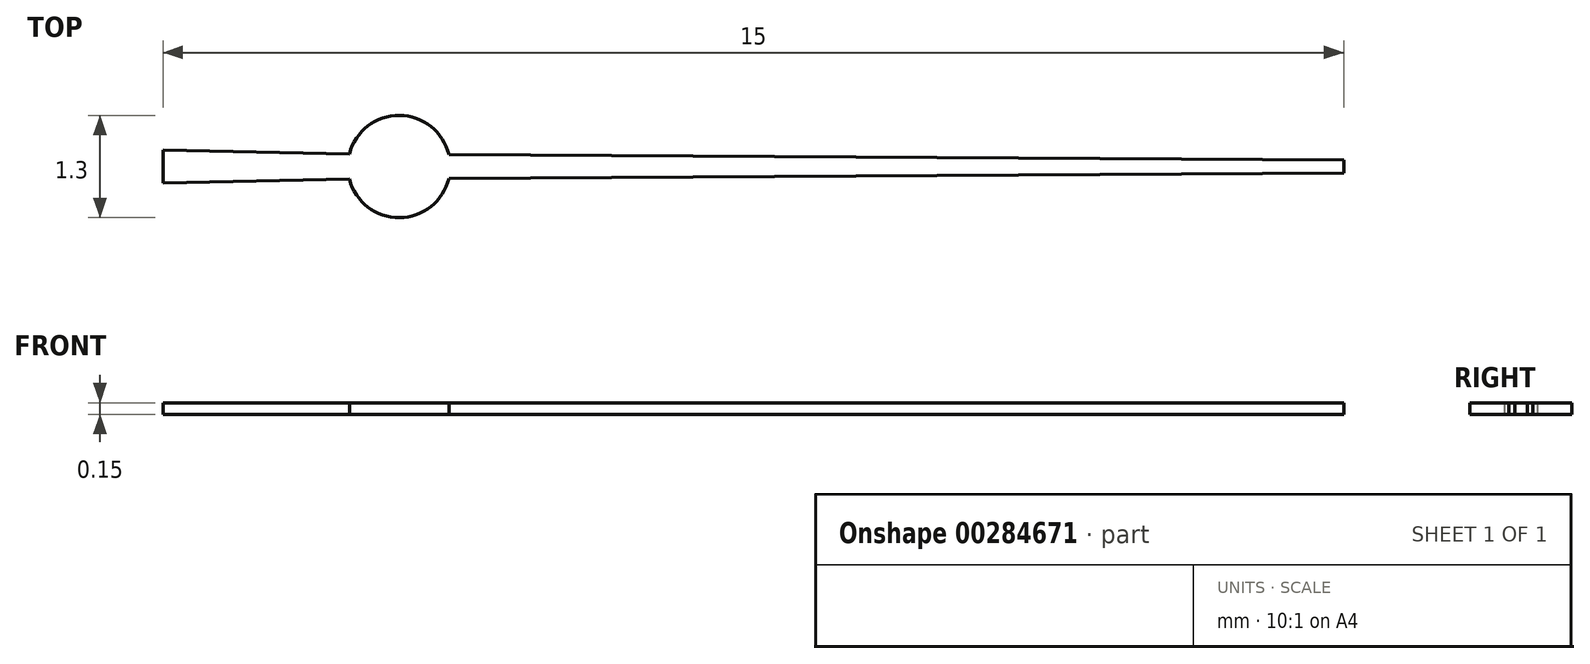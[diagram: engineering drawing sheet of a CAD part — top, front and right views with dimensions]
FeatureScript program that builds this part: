
annotation { "Feature Type Name" : "Feature", "Feature Type Description" : "" }
export const myFeature = defineFeature(function(context is Context, id is Id, definition is map)
    precondition{}
    {
        {
            var Q0;
            Q0=qCreatedBy(makeId("Top.planeOp"),FACE);
            var sketch = newSketch(context, id + "F0", { "sketchPlane" : qUnion([Q0])});
            skArc(sketch, "E0", {"start": v(0.63, 0.15) * mm, "mid": v(0, 0.65) * mm, "end": v(-0.63, 0.16) * mm});
            skLineSegment(sketch, "E1", {"start": v(0, 0) * mm, "end": v(12, 0) * mm, "construction": true});
            skLineSegment(sketch, "E2", {"start": v(0, 0) * mm, "end": v(-3, 0) * mm, "construction": true});
            skLineSegment(sketch, "E3", {"start": v(-3, 0) * mm, "end": v(-3, -0.21) * mm});
            skLineSegment(sketch, "E4.MirrorCS", {"start": v(-3, 0) * mm, "end": v(-3, 0.2) * mm});
            skLineSegment(sketch, "E5", {"start": v(12, 0) * mm, "end": v(12, -0.08) * mm});
            skLineSegment(sketch, "E6.MirrorCS", {"start": v(12, 0) * mm, "end": v(12, 0.08) * mm});
            skLineSegment(sketch, "E7.0", {"start": v(0, -0.16) * mm, "end": v(-3.75, -0.16) * mm, "construction": true});
            skLineSegment(sketch, "E8.0", {"start": v(0, -0.15) * mm, "end": v(16.5, -0.15) * mm, "construction": true});
            skLineSegment(sketch, "E9", {"start": v(-3, -0.21) * mm, "end": v(-0.63, -0.16) * mm});
            skLineSegment(sketch, "E10.MirrorCS", {"start": v(-3, 0.2) * mm, "end": v(-0.63, 0.16) * mm});
            skLineSegment(sketch, "E11", {"start": v(0.63, -0.15) * mm, "end": v(12, -0.08) * mm});
            skLineSegment(sketch, "E12.MirrorCS", {"start": v(0.63, 0.15) * mm, "end": v(12, 0.08) * mm});
            skArc(sketch, "E13.trimOffspring", {"start": v(-0.63, -0.16) * mm, "mid": v(0, -0.65) * mm, "end": v(0.63, -0.15) * mm});
            skSolve(sketch);
        }
        {
            var Q0;
            Q0 = qSketchRegion(id + "F0", true);
            extrude(context, id + "F1", {"entities" : qUnion([Q0]), "depth" : 0.15 * mm, "offsetDistance" : 25 * mm});
        }
    });
